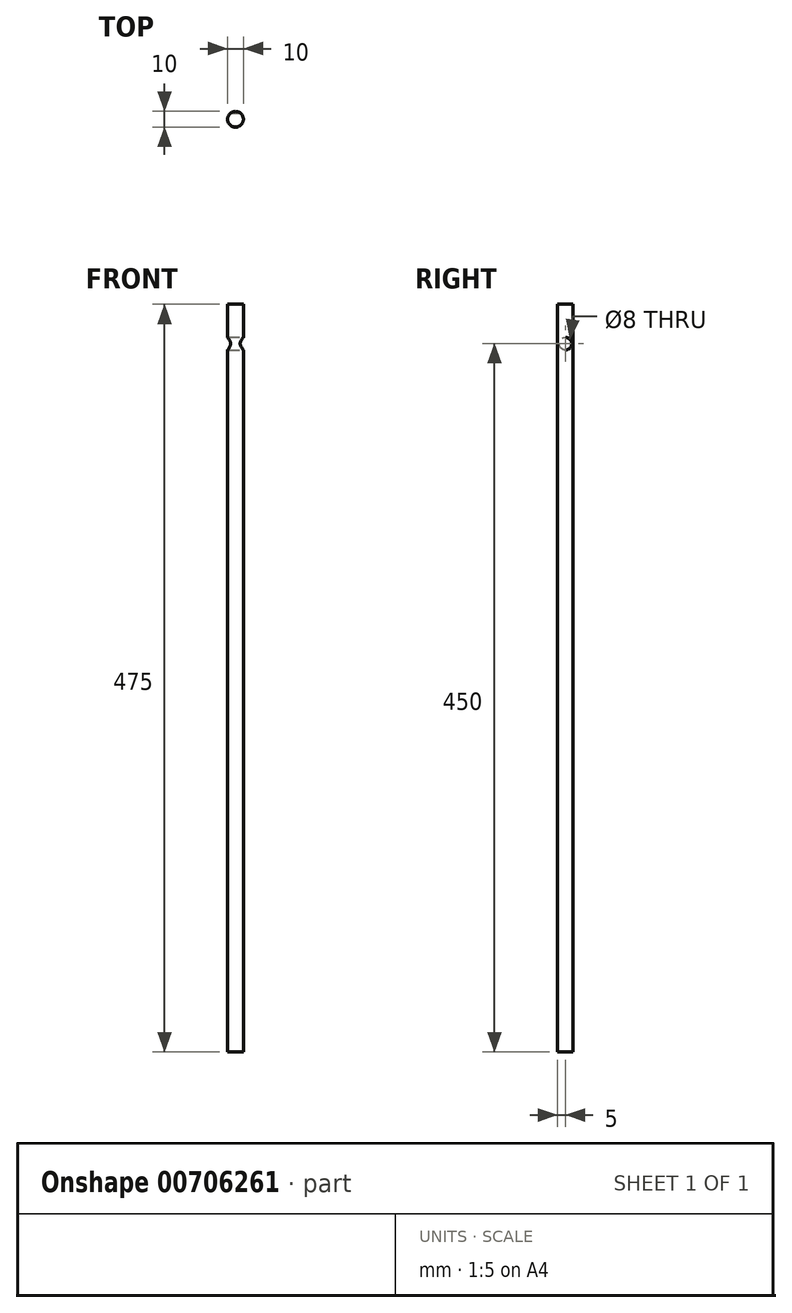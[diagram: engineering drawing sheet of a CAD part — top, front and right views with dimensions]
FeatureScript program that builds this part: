
annotation { "Feature Type Name" : "Feature", "Feature Type Description" : "" }
export const myFeature = defineFeature(function(context is Context, id is Id, definition is map)
    precondition{}
    {
        {
            var Q0;
            Q0=qCreatedBy(makeId("Top.planeOp"),FACE);
            var sketch = newSketch(context, id + "F0", { "sketchPlane" : qUnion([Q0])});
            skCircle(sketch, "E0", {"center": v(0, 0) * mm, "radius": 5 * mm});
            skSolve(sketch);
        }
        {
            var Q0;
            Q0 = qSketchRegion(id + "F0", true);
            extrude(context, id + "F1", {"entities" : qUnion([Q0]), "depth" : 475 * mm, "offsetDistance" : 25 * mm});
        }
        {
            var Q0;
            Q0=qCreatedBy(makeId("Right.planeOp"),FACE);
            var sketch = newSketch(context, id + "F2", { "sketchPlane" : qUnion([Q0])});
            skLineSegment(sketch, "E1", {"start": v(0, 0) * mm, "end": v(0, 450) * mm});
            skCircle(sketch, "E2", {"center": v(0, 450) * mm, "radius": 4 * mm});
            skSolve(sketch);
        }
        {
            var Q0;
            Q0=sQuery(id+"F2.wireOp",VERTEX,"E2.center");
            var Q1;
            Q1=makeQuery(id+"F1.opExtrude","SWEPT_BODY",BODY,{"disambiguationData":[OSD([sQuery(id+"F0.wireOp",EDGE,"E0")])]});
            hole(context, id + "F3", {"style" : HoleStyle.SIMPLE, "endStyle" : HoleEndStyle.THROUGH, "holeDiameter" : 8 * mm, "majorDiameter" : 5 * mm, "isTappedThrough" : true, "tappedDepth" : 12 * mm, "tapClearance" : 3, "locations" : qUnion([Q0]), "scope" : qUnion([Q1])});
        }
        {
            var Q0;
            Q0=sQuery(id+"F2.wireOp",VERTEX,"E2.center");
            var Q1;
            Q1=makeQuery(id+"F1.opExtrude","SWEPT_BODY",BODY,{"disambiguationData":[OSD([sQuery(id+"F0.wireOp",EDGE,"E0")])]});
            hole(context, id + "F4", {"style" : HoleStyle.SIMPLE, "endStyle" : HoleEndStyle.THROUGH, "oppositeDirection" : true, "holeDiameter" : 8 * mm, "majorDiameter" : 5 * mm, "isTappedThrough" : true, "tappedDepth" : 12 * mm, "tapClearance" : 3, "locations" : qUnion([Q0]), "scope" : qUnion([Q1])});
        }
    });
